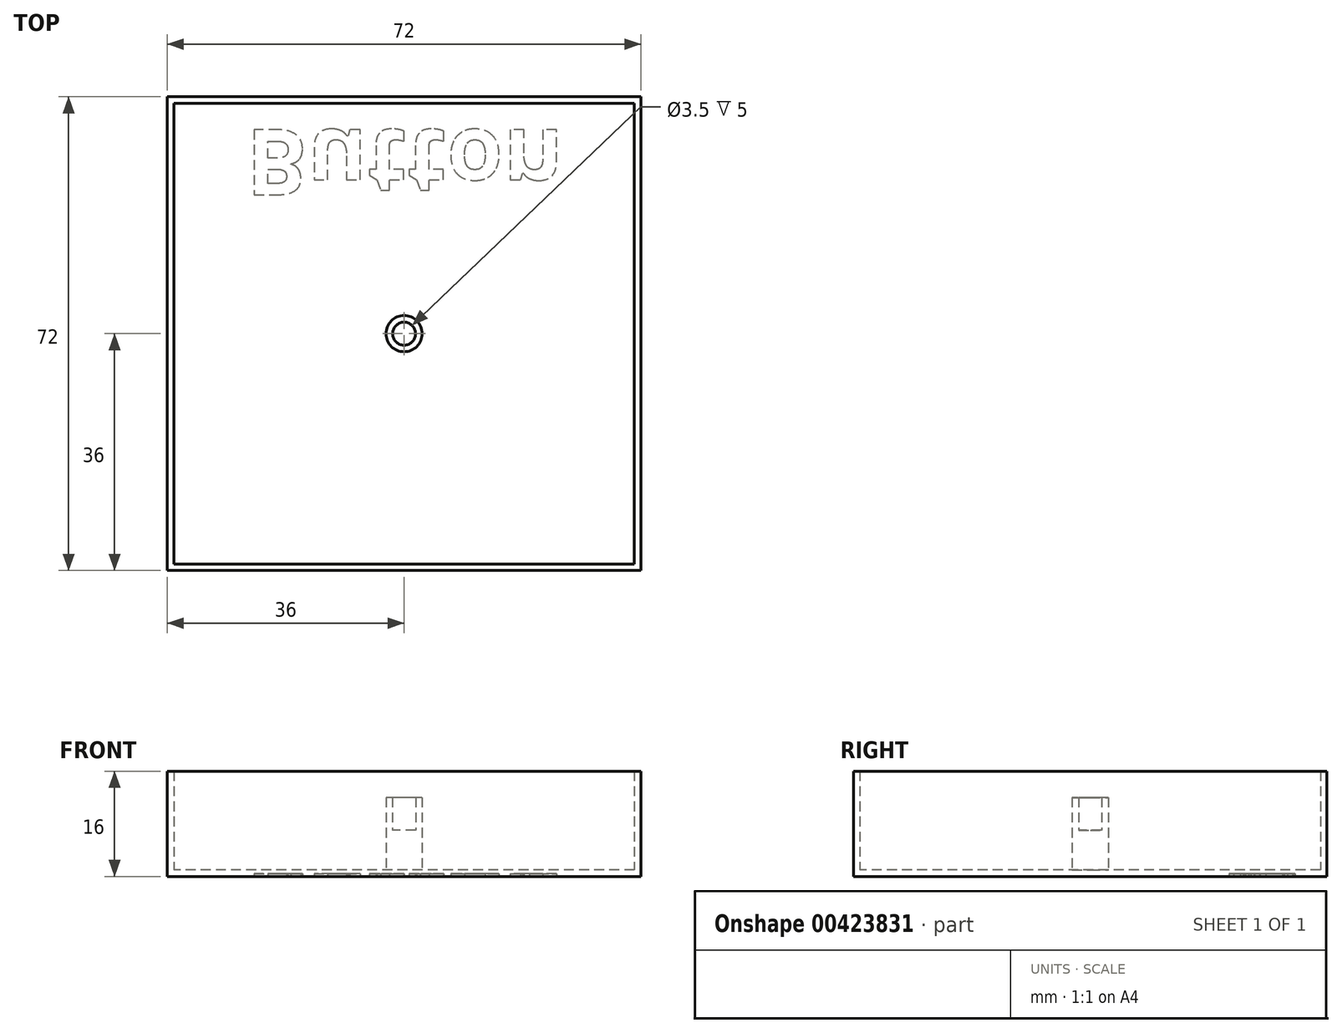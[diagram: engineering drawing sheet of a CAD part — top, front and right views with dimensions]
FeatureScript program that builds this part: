
annotation { "Feature Type Name" : "Feature", "Feature Type Description" : "" }
export const myFeature = defineFeature(function(context is Context, id is Id, definition is map)
    precondition{}
    {
        {
            var Q0;
            Q0=qCreatedBy(makeId("Top.planeOp"),FACE);
            var sketch = newSketch(context, id + "F0", { "sketchPlane" : qUnion([Q0])});
            skLineSegment(sketch, "E0.bottom", {"start": v(-36, 36) * mm, "end": v(36, 36) * mm});
            skLineSegment(sketch, "E0.top", {"start": v(-36, -36) * mm, "end": v(36, -36) * mm});
            skLineSegment(sketch, "E0.left", {"start": v(-36, 36) * mm, "end": v(-36, -36) * mm});
            skLineSegment(sketch, "E0.right", {"start": v(36, 36) * mm, "end": v(36, -36) * mm});
            skPoint(sketch, "E0.middle", {"position": v(0, 0) * mm});
            skSolve(sketch);
        }
        {
            var Q0;
            Q0 = qSketchRegion(id + "F0", true);
            extrude(context, id + "F1", {"entities" : qUnion([Q0]), "depth" : 1 * mm});
        }
        {
            var Q0;
            Q0=makeQuery(id+"F1.opExtrude","CAP_FACE",FACE,{"disambiguationData":[OSD([sQuery(id+"F0.wireOp",EDGE,"E0.bottom"),sQuery(id+"F0.wireOp",EDGE,"E0.top"),sQuery(id+"F0.wireOp",EDGE,"E0.left"),sQuery(id+"F0.wireOp",EDGE,"E0.right")])],"isStart":false});
            var sketch = newSketch(context, id + "F2", { "sketchPlane" : qUnion([Q0])});
            skCircle(sketch, "E1", {"center": v(0, 0) * mm, "radius": 2.75 * mm});
            skCircle(sketch, "E2", {"center": v(0, 0) * mm, "radius": 1.75 * mm});
            skSolve(sketch);
        }
        {
            var Q0;
            Q0 = qSketchRegion(id + "F2", true);
            extrude(context, id + "F3", {"entities" : qUnion([Q0]), "operationType" : NewBodyOperationType.ADD, "depth" : 11 * mm});
        }
        {
            var Q0;
            {var subQ0=sQuery(id+"F0.wireOp",EDGE,"E0.left");var subQ1=sQuery(id+"F0.wireOp",EDGE,"E0.top");var subQ2=sQuery(id+"F0.wireOp",EDGE,"E0.right");var subQ3=sQuery(id+"F0.wireOp",EDGE,"E0.bottom");Q0=makeQuery(id+"F3.boolean.opBoolean","SPLIT",FACE,{"disambiguationData":[TD([makeQuery(id+"F1.opExtrude","SWEPT_FACE",FACE,{"disambiguationData":[OSD([subQ3])]})])],"derivedFrom":makeQuery(id+"F1.opExtrude","CAP_FACE",FACE,{"disambiguationData":[OSD([subQ3,subQ1,subQ0,subQ2])],"isStart":false})});}
            var sketch = newSketch(context, id + "F4", { "sketchPlane" : qUnion([Q0])});
            skLineSegment(sketch, "E3.bottom", {"start": v(-36, 36) * mm, "end": v(-35, 36) * mm});
            skLineSegment(sketch, "E3.top", {"start": v(-36, -36) * mm, "end": v(-35, -36) * mm});
            skLineSegment(sketch, "E3.left", {"start": v(-36, 36) * mm, "end": v(-36, -36) * mm});
            skLineSegment(sketch, "E3.right", {"start": v(-35, 36) * mm, "end": v(-35, -36) * mm});
            skLineSegment(sketch, "E4.bottom", {"start": v(36, 36) * mm, "end": v(35, 36) * mm});
            skLineSegment(sketch, "E4.top", {"start": v(36, -36) * mm, "end": v(35, -36) * mm});
            skLineSegment(sketch, "E4.left", {"start": v(36, 36) * mm, "end": v(36, -36) * mm});
            skLineSegment(sketch, "E4.right", {"start": v(35, 36) * mm, "end": v(35, -36) * mm});
            skLineSegment(sketch, "E5.bottom", {"start": v(35, -36) * mm, "end": v(-35, -36) * mm});
            skLineSegment(sketch, "E5.top", {"start": v(35, -35) * mm, "end": v(-35, -35) * mm});
            skLineSegment(sketch, "E5.left", {"start": v(35, -36) * mm, "end": v(35, -35) * mm});
            skLineSegment(sketch, "E5.right", {"start": v(-35, -36) * mm, "end": v(-35, -35) * mm});
            skLineSegment(sketch, "E6.bottom", {"start": v(-35, 36) * mm, "end": v(35, 36) * mm});
            skLineSegment(sketch, "E6.top", {"start": v(-35, 35) * mm, "end": v(35, 35) * mm});
            skLineSegment(sketch, "E6.left", {"start": v(-35, 36) * mm, "end": v(-35, 35) * mm});
            skLineSegment(sketch, "E6.right", {"start": v(35, 36) * mm, "end": v(35, 35) * mm});
            skSolve(sketch);
        }
        {
            var Q0;
            Q0 = qSketchRegion(id + "F4", true);
            extrude(context, id + "F5", {"entities" : qUnion([Q0]), "operationType" : NewBodyOperationType.ADD, "depth" : 15 * mm});
        }
        {
            var Q0;
            Q0=makeQuery(id+"F3.boolean.opBoolean","SPLIT",FACE,{"disambiguationData":[TD([makeQuery(id+"F3.opExtrude","SWEPT_FACE",FACE,{"disambiguationData":[OSD([sQuery(id+"F2.wireOp",EDGE,"E2")])]})])],"derivedFrom":makeQuery(id+"F1.opExtrude","CAP_FACE",FACE,{"disambiguationData":[OSD([sQuery(id+"F0.wireOp",EDGE,"E0.bottom"),sQuery(id+"F0.wireOp",EDGE,"E0.top"),sQuery(id+"F0.wireOp",EDGE,"E0.left"),sQuery(id+"F0.wireOp",EDGE,"E0.right")])],"isStart":false})});
            var sketch = newSketch(context, id + "F6", { "sketchPlane" : qUnion([Q0])});
            skCircle(sketch, "E7", {"center": v(0, 0) * mm, "radius": 1.75 * mm});
            skSolve(sketch);
        }
        {
            var Q0;
            Q0 = qSketchRegion(id + "F6", true);
            extrude(context, id + "F7", {"entities" : qUnion([Q0]), "operationType" : NewBodyOperationType.ADD, "depth" : 6 * mm});
        }
        {
            var Q0;
            Q0=makeQuery(id+"F1.opExtrude","CAP_FACE",FACE,{"disambiguationData":[OSD([sQuery(id+"F0.wireOp",EDGE,"E0.bottom"),sQuery(id+"F0.wireOp",EDGE,"E0.top"),sQuery(id+"F0.wireOp",EDGE,"E0.left"),sQuery(id+"F0.wireOp",EDGE,"E0.right")])],"isStart":true});
            var sketch = newSketch(context, id + "F8", { "sketchPlane" : qUnion([Q0])});
            skText(sketch, "E8", { "text": "Button", "fontName": "OpenSans-Bold.ttf"});
            const initialGuessF8  = {"E8": [-0.02405, -0.031, 1, 0, 0.01]};
            skSetInitialGuess(sketch, initialGuessF8);
            skSolve(sketch);
        }
        {
            var Q0;
            Q0 = qSketchRegion(id + "F8", true);
            extrude(context, id + "F9", {"entities" : qUnion([Q0]), "operationType" : NewBodyOperationType.REMOVE, "oppositeDirection" : true, "depth" : 0.4 * mm});
        }
    });
